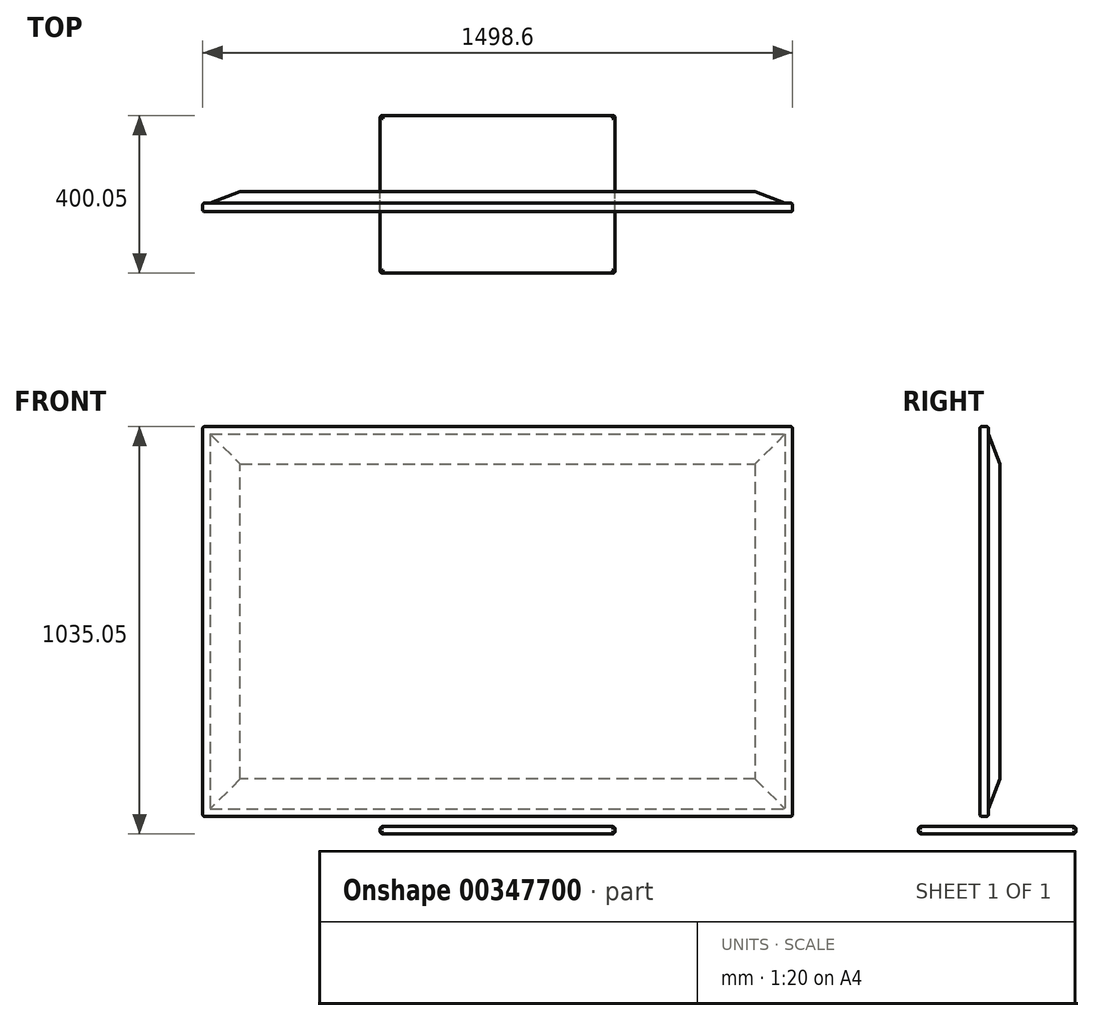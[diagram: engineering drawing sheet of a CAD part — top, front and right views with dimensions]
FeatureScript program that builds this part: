
annotation { "Feature Type Name" : "Feature", "Feature Type Description" : "" }
export const myFeature = defineFeature(function(context is Context, id is Id, definition is map)
    precondition{}
    {
        {
            var Q0;
            Q0=qCreatedBy(makeId("Front.planeOp"),FACE);
            var sketch = newSketch(context, id + "F0", { "sketchPlane" : qUnion([Q0])});
            skLineSegment(sketch, "E0.bottom", {"start": v(-749.3, 990.6) * mm, "end": v(749.3, 990.6) * mm});
            skLineSegment(sketch, "E0.top", {"start": v(-749.3, 0) * mm, "end": v(749.3, 0) * mm});
            skLineSegment(sketch, "E0.left", {"start": v(-749.3, 990.6) * mm, "end": v(-749.3, 0) * mm});
            skLineSegment(sketch, "E0.right", {"start": v(749.3, 990.6) * mm, "end": v(749.3, 0) * mm});
            skLineSegment(sketch, "E1", {"start": v(0, 0) * mm, "end": v(0, 851.49) * mm, "construction": true});
            skPoint(sketch, "E1.endSnap0", {"position": v(0, 990.6) * mm});
            skSolve(sketch);
        }
        {
            var Q0;
            Q0 = qSketchRegion(id + "F0", true);
            extrude(context, id + "F1", {"entities" : qUnion([Q0]), "depth" : 22.22 * mm});
        }
        {
            var Q0;
            Q0=makeQuery(id+"F1.opExtrude","CAP_FACE",FACE,{"disambiguationData":[OSD([sQuery(id+"F0.wireOp",EDGE,"E0.bottom"),sQuery(id+"F0.wireOp",EDGE,"E0.top"),sQuery(id+"F0.wireOp",EDGE,"E0.left"),sQuery(id+"F0.wireOp",EDGE,"E0.right")])],"isStart":true});
            var sketch = newSketch(context, id + "F2", { "sketchPlane" : qUnion([Q0])});
            skLineSegment(sketch, "E2.0", {"start": v(-730.25, 971.55) * mm, "end": v(-730.25, 19.05) * mm});
            skLineSegment(sketch, "E2.1", {"start": v(730.25, 971.55) * mm, "end": v(-730.25, 971.55) * mm});
            skLineSegment(sketch, "E2.2", {"start": v(730.25, 971.55) * mm, "end": v(730.25, 19.05) * mm});
            skLineSegment(sketch, "E2.3", {"start": v(730.25, 19.05) * mm, "end": v(-730.25, 19.05) * mm});
            skSolve(sketch);
        }
        {
            var Q0;
            Q0 = qSketchRegion(id + "F2", true);
            extrude(context, id + "F3", {"entities" : qUnion([Q0]), "operationType" : NewBodyOperationType.ADD, "depth" : 28.57 * mm});
        }
        {
            var Q0;
            Q0=makeQuery(id+"F3.opExtrude","CAP_EDGE",EDGE,{"disambiguationData":[OSD([sQuery(id+"F2.wireOp",EDGE,"E2.1")])],"isStart":false});
            var Q1;
            Q1=makeQuery(id+"F3.opExtrude","CAP_EDGE",EDGE,{"disambiguationData":[OSD([sQuery(id+"F2.wireOp",EDGE,"E2.0")])],"isStart":false});
            var Q2;
            Q2=makeQuery(id+"F3.opExtrude","CAP_EDGE",EDGE,{"disambiguationData":[OSD([sQuery(id+"F2.wireOp",EDGE,"E2.2")])],"isStart":false});
            var Q3;
            Q3=makeQuery(id+"F3.opExtrude","CAP_EDGE",EDGE,{"disambiguationData":[OSD([sQuery(id+"F2.wireOp",EDGE,"E2.3")])],"isStart":false});
            chamfer(context, id + "F4", {"entities" : qUnion([Q0, Q1, Q2, Q3]), "chamferType" : ChamferType.TWO_OFFSETS, "width1" : 76.2 * mm, "oppositeDirection" : false, "width2" : 28.57 * mm, "tangentPropagation" : true});
        }
        {
            var Q0;
            Q0=makeQuery(id+"F1.opExtrude","SWEPT_FACE",FACE,{"disambiguationData":[OSD([sQuery(id+"F0.wireOp",EDGE,"E0.top")])]});
            cPlane(context, id + "F5", {"entities" : qUnion([Q0]), "cplaneType" : CPlaneType.OFFSET, "offset" : 25.4 * mm, "width" : 152.4 * mm, "height" : 152.4 * mm});
        }
        {
            var Q0;
            Q0=makeQuery(id+"F1.opExtrude","CAP_FACE",FACE,{"disambiguationData":[OSD([sQuery(id+"F0.wireOp",EDGE,"E0.bottom"),sQuery(id+"F0.wireOp",EDGE,"E0.top"),sQuery(id+"F0.wireOp",EDGE,"E0.left"),sQuery(id+"F0.wireOp",EDGE,"E0.right")])],"isStart":false});
            cPlane(context, id + "F6", {"entities" : qUnion([Q0]), "cplaneType" : CPlaneType.OFFSET, "offset" : 155.57 * mm, "width" : 152.4 * mm, "height" : 152.4 * mm});
        }
        {
            var Q0;
            Q0=qCreatedBy(id+"F5.planeOp",FACE);
            var sketch = newSketch(context, id + "F7", { "sketchPlane" : qUnion([Q0])});
            skLineSegment(sketch, "E3.bottom", {"start": v(-298.45, 177.8) * mm, "end": v(298.45, 177.8) * mm});
            skLineSegment(sketch, "E3.top", {"start": v(-298.45, -222.25) * mm, "end": v(298.45, -222.25) * mm});
            skLineSegment(sketch, "E3.left", {"start": v(-298.45, 177.8) * mm, "end": v(-298.45, -222.25) * mm});
            skLineSegment(sketch, "E3.right", {"start": v(298.45, 177.8) * mm, "end": v(298.45, -222.25) * mm});
            skLineSegment(sketch, "E4", {"start": v(0, -222.25) * mm, "end": v(0, 124.9) * mm, "construction": true});
            skSolve(sketch);
        }
        {
            var Q0;
            Q0 = qSketchRegion(id + "F7", true);
            extrude(context, id + "F8", {"entities" : qUnion([Q0]), "depth" : 19.05 * mm});
        }
        {
            var Q0;
            Q0=makeQuery(id+"F8.opExtrude","SWEPT_EDGE",EDGE,{"disambiguationData":[OSD([sQuery(id+"F7.wireOp",EDGE,"E3.bottom"),sQuery(id+"F7.wireOp",EDGE,"E3.left")])]});
            var Q1;
            Q1=makeQuery(id+"F8.opExtrude","SWEPT_EDGE",EDGE,{"disambiguationData":[OSD([sQuery(id+"F7.wireOp",EDGE,"E3.bottom"),sQuery(id+"F7.wireOp",EDGE,"E3.right")])]});
            var Q2;
            Q2=makeQuery(id+"F8.opExtrude","SWEPT_EDGE",EDGE,{"disambiguationData":[OSD([sQuery(id+"F7.wireOp",EDGE,"E3.top"),sQuery(id+"F7.wireOp",EDGE,"E3.right")])]});
            var Q3;
            Q3=makeQuery(id+"F8.opExtrude","SWEPT_EDGE",EDGE,{"disambiguationData":[OSD([sQuery(id+"F7.wireOp",EDGE,"E3.top"),sQuery(id+"F7.wireOp",EDGE,"E3.left")])]});
            fillet(context, id + "F9", {"entities" : qUnion([Q0, Q1, Q2, Q3]), "radius" : 5.08 * mm, "tangentPropagation" : true, "allowEdgeOverflow" : false});
        }
        {
            var Q0;
            Q0=makeQuery(id+"F8.opExtrude","CAP_EDGE",EDGE,{"disambiguationData":[OSD([sQuery(id+"F7.wireOp",EDGE,"E3.top")])],"isStart":true});
            var Q1;
            Q1=makeQuery(id+"F8.opExtrude","CAP_EDGE",EDGE,{"disambiguationData":[OSD([sQuery(id+"F7.wireOp",EDGE,"E3.top")])],"isStart":false});
            fillet(context, id + "F10", {"entities" : qUnion([Q0, Q1]), "radius" : 7.62 * mm, "tangentPropagation" : true, "allowEdgeOverflow" : false});
        }
        {
            var Q0;
            Q0=makeQuery(id+"F1.opExtrude","SWEPT_EDGE",EDGE,{"disambiguationData":[OSD([sQuery(id+"F0.wireOp",EDGE,"E0.bottom"),sQuery(id+"F0.wireOp",EDGE,"E0.right")])]});
            var Q1;
            Q1=makeQuery(id+"F1.opExtrude","SWEPT_EDGE",EDGE,{"disambiguationData":[OSD([sQuery(id+"F0.wireOp",EDGE,"E0.bottom"),sQuery(id+"F0.wireOp",EDGE,"E0.left")])]});
            var Q2;
            Q2=makeQuery(id+"F1.opExtrude","SWEPT_EDGE",EDGE,{"disambiguationData":[OSD([sQuery(id+"F0.wireOp",EDGE,"E0.top"),sQuery(id+"F0.wireOp",EDGE,"E0.right")])]});
            var Q3;
            Q3=makeQuery(id+"F1.opExtrude","SWEPT_EDGE",EDGE,{"disambiguationData":[OSD([sQuery(id+"F0.wireOp",EDGE,"E0.top"),sQuery(id+"F0.wireOp",EDGE,"E0.left")])]});
            fillet(context, id + "F11", {"entities" : qUnion([Q0, Q1, Q2, Q3]), "radius" : 5.08 * mm, "tangentPropagation" : true, "allowEdgeOverflow" : false});
        }
        {
            var Q0;
            Q0=makeQuery(id+"F1.opExtrude","CAP_EDGE",EDGE,{"disambiguationData":[OSD([sQuery(id+"F0.wireOp",EDGE,"E0.bottom")])],"isStart":false});
            var Q1;
            Q1=makeQuery(id+"F1.opExtrude","CAP_EDGE",EDGE,{"disambiguationData":[OSD([sQuery(id+"F0.wireOp",EDGE,"E0.bottom")])],"isStart":true});
            fillet(context, id + "F12", {"entities" : qUnion([Q0, Q1]), "radius" : 5.08 * mm, "tangentPropagation" : true, "allowEdgeOverflow" : false});
        }
    });
